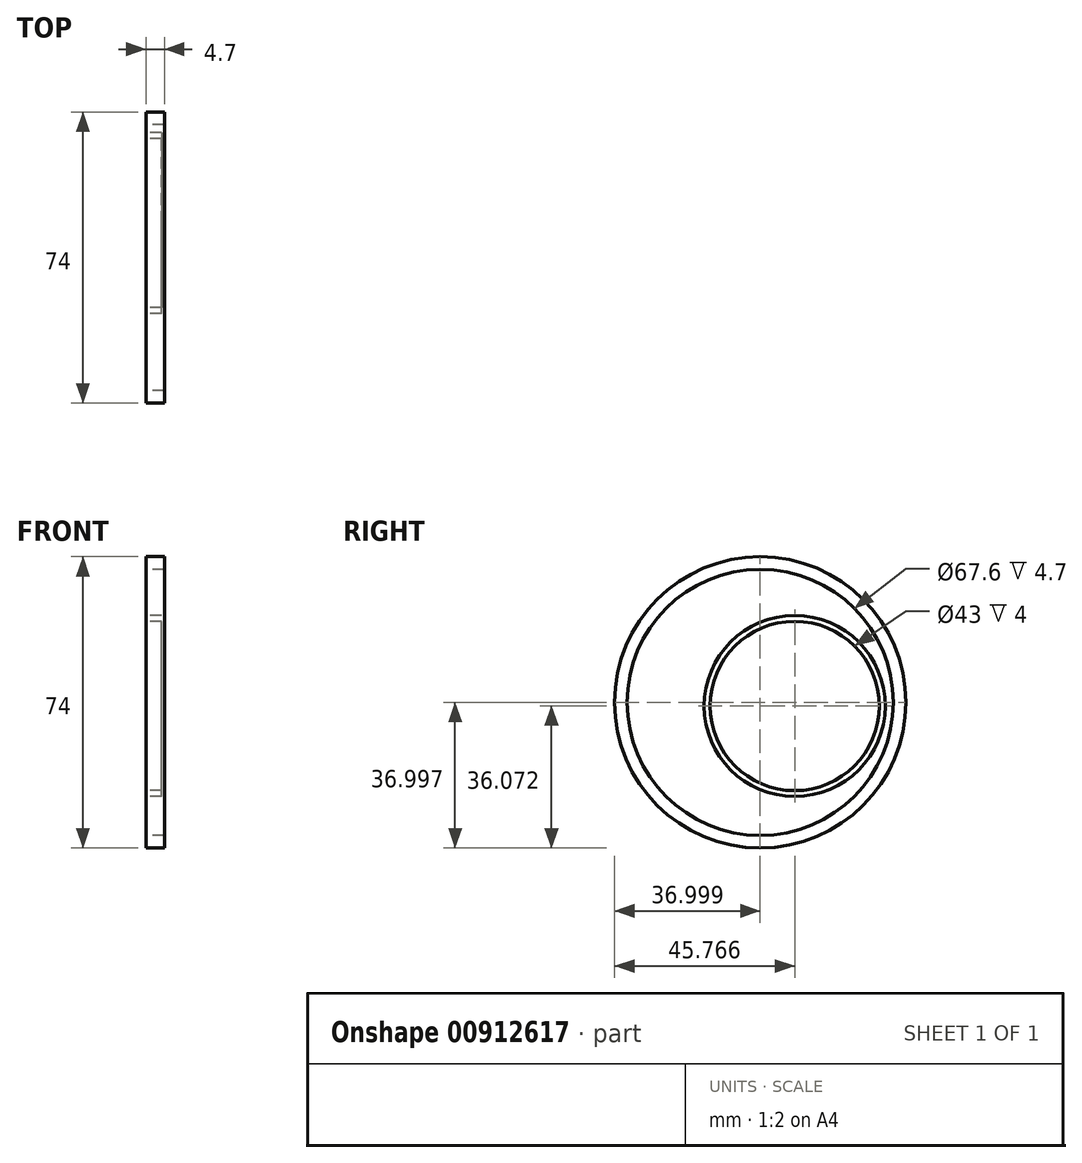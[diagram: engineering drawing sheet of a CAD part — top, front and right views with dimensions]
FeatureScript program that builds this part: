
annotation { "Feature Type Name" : "Feature", "Feature Type Description" : "" }
export const myFeature = defineFeature(function(context is Context, id is Id, definition is map)
    precondition{}
    {
        {
            var Q0;
            Q0=qCreatedBy(makeId("Right.planeOp"),FACE);
            var sketch = newSketch(context, id + "F0", { "sketchPlane" : qUnion([Q0])});
            skCircle(sketch, "E0", {"center": v(-166.56, -19.19) * mm, "radius": 23 * mm});
            skCircle(sketch, "E1.0", {"center": v(-166.56, -19.19) * mm, "radius": 21.5 * mm});
            skSolve(sketch);
        }
        {
            var Q0;
            Q0 = qSketchRegion(id + "F0", true);
            extrude(context, id + "F1", {"entities" : qUnion([Q0]), "depth" : 4 * mm, "offsetDistance" : 25.4 * mm});
        }
        {
            var Q0;
            Q0=qCreatedBy(makeId("Right.planeOp"),FACE);
            var sketch = newSketch(context, id + "F2", { "sketchPlane" : qUnion([Q0])});
            skCircle(sketch, "E2", {"center": v(-175.33, -18.26) * mm, "radius": 37 * mm});
            skCircle(sketch, "E3.0", {"center": v(-175.33, -18.26) * mm, "radius": 33.8 * mm});
            skPoint(sketch, "E4.0", {"position": v(-166.56, -19.19) * mm});
            skSolve(sketch);
        }
        {
            var Q0;
            Q0 = qSketchRegion(id + "F2", true);
            extrude(context, id + "F3", {"entities" : qUnion([Q0]), "depth" : 4.7 * mm, "offsetDistance" : 25.4 * mm});
        }
    });
